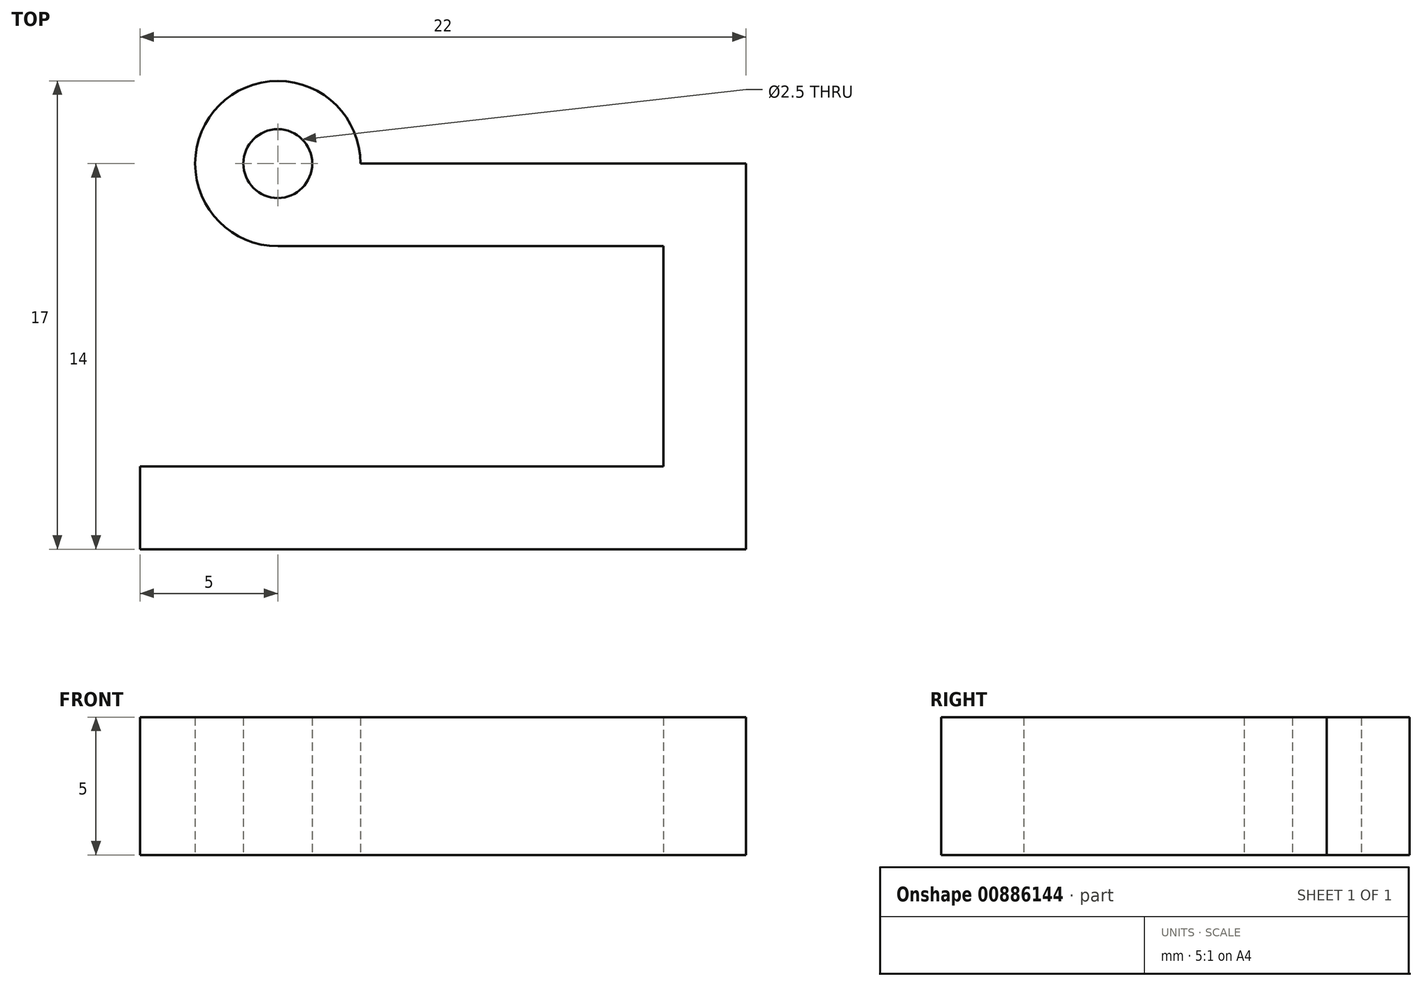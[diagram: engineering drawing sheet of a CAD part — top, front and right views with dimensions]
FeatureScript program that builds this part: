
annotation { "Feature Type Name" : "Feature", "Feature Type Description" : "" }
export const myFeature = defineFeature(function(context is Context, id is Id, definition is map)
    precondition{}
    {
        {
            var Q0;
            Q0=qCreatedBy(makeId("Top.planeOp"),FACE);
            var sketch = newSketch(context, id + "F0", { "sketchPlane" : qUnion([Q0])});
            skLineSegment(sketch, "E0.bottom", {"start": v(2.15, 8.42) * mm, "end": v(16.15, 8.42) * mm});
            skLineSegment(sketch, "E0.top", {"start": v(-5.85, -5.58) * mm, "end": v(16.15, -5.58) * mm});
            skLineSegment(sketch, "E0.right", {"start": v(16.15, 8.42) * mm, "end": v(16.15, -5.58) * mm});
            skLineSegment(sketch, "E1.bottom", {"start": v(-0.85, 5.42) * mm, "end": v(13.15, 5.42) * mm});
            skLineSegment(sketch, "E1.top", {"start": v(-5.85, -2.58) * mm, "end": v(13.15, -2.58) * mm});
            skLineSegment(sketch, "E1.right", {"start": v(13.15, 5.42) * mm, "end": v(13.15, -2.58) * mm});
            skLineSegment(sketch, "E2.trimOffspring", {"start": v(-5.85, -2.58) * mm, "end": v(-5.85, -5.58) * mm});
            skArc(sketch, "E3", {"start": v(2.15, 8.42) * mm, "mid": v(-2.97, 10.54) * mm, "end": v(-0.85, 5.42) * mm});
            skCircle(sketch, "E4", {"center": v(-0.85, 8.42) * mm, "radius": 1.25 * mm});
            skSolve(sketch);
        }
        {
            var Q0;
            Q0=makeQuery(id+"F0.imprint","IMPRINT",FACE,{"disambiguationData":[TD([[makeQuery(id+"F0.imprint","IMPRINT",EDGE,{"derivedFrom":sQuery(id+"F0.wireOp",EDGE,"E0.bottom")}),-1.0]])]});
            extrude(context, id + "F1", {"entities" : qUnion([Q0]), "depth" : 5 * mm, "offsetDistance" : 25 * mm});
        }
    });
